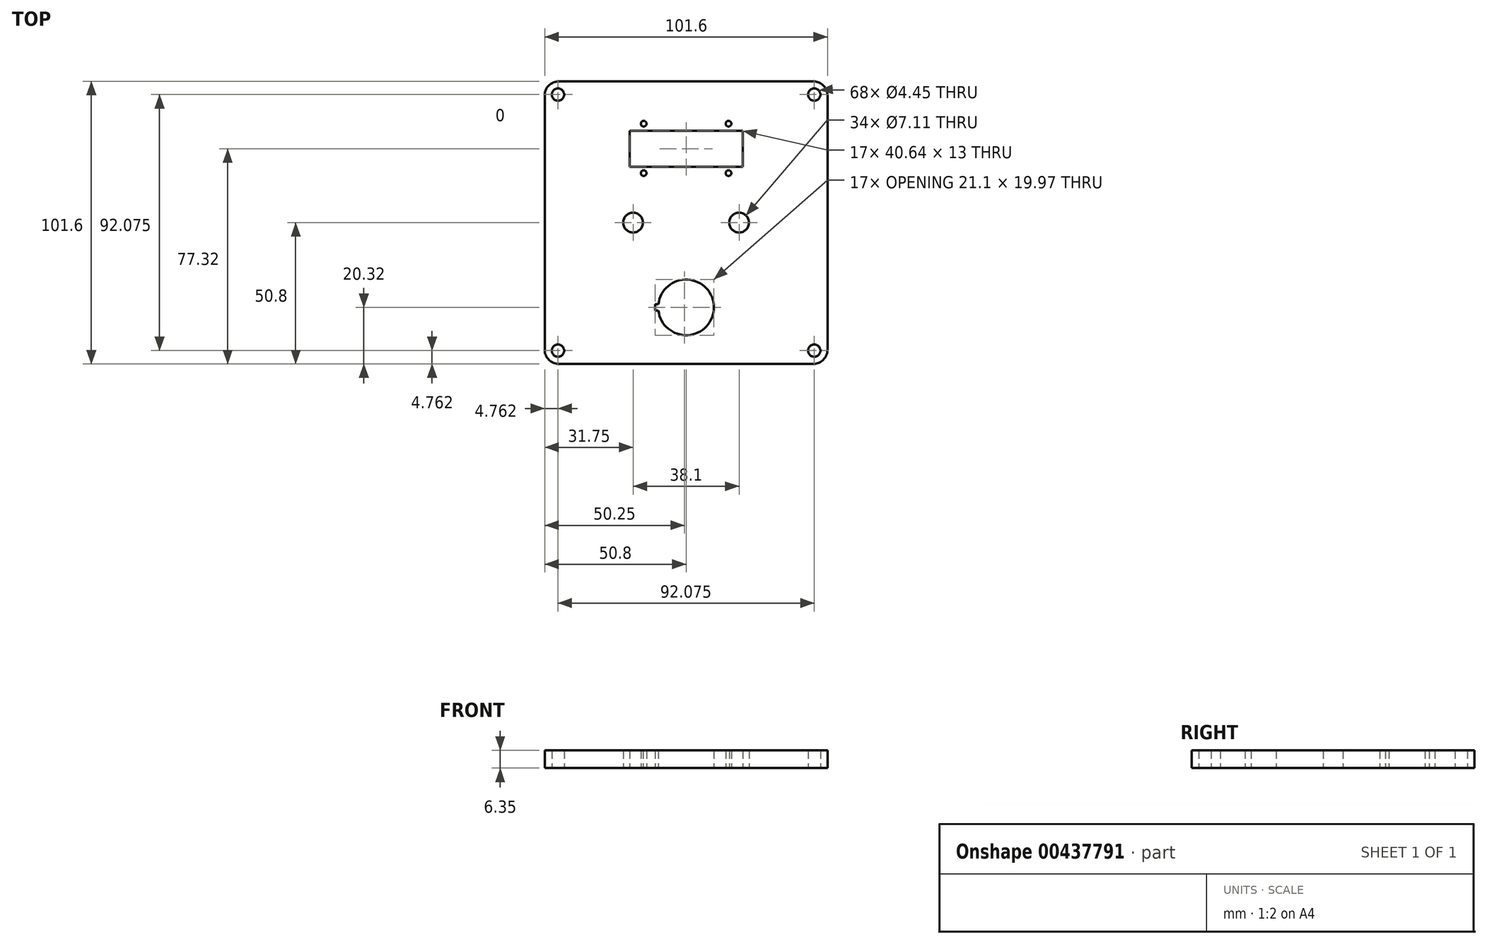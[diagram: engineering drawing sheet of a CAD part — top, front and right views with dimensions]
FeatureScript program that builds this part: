
annotation { "Feature Type Name" : "Feature", "Feature Type Description" : "" }
export const myFeature = defineFeature(function(context is Context, id is Id, definition is map)
    precondition{}
    {
        {
            var Q0;
            Q0=qCreatedBy(makeId("Top.planeOp"),FACE);
            var sketch = newSketch(context, id + "F0", { "sketchPlane" : qUnion([Q0])});
            skLineSegment(sketch, "E0.bottom", {"start": v(-45.72, 50.8) * mm, "end": v(45.72, 50.8) * mm});
            skLineSegment(sketch, "E0.top", {"start": v(-45.72, -50.8) * mm, "end": v(45.72, -50.8) * mm});
            skLineSegment(sketch, "E0.left", {"start": v(-50.8, 45.72) * mm, "end": v(-50.8, -45.72) * mm});
            skLineSegment(sketch, "E0.right", {"start": v(50.8, 45.72) * mm, "end": v(50.8, -45.72) * mm});
            skCircle(sketch, "E1", {"center": v(-46.04, 46.04) * mm, "radius": 2.22 * mm});
            skCircle(sketch, "E2.0.1.0", {"center": v(-46.04, -46.04) * mm, "radius": 2.22 * mm});
            skCircle(sketch, "E2.1.0.0", {"center": v(46.04, 46.04) * mm, "radius": 2.22 * mm});
            skCircle(sketch, "E2.1.1.0", {"center": v(46.04, -46.04) * mm, "radius": 2.22 * mm});
            skLineSegment(sketch, "E2.direction1", {"start": v(-46.04, 46.04) * mm, "end": v(46.04, 46.04) * mm, "construction": true});
            skLineSegment(sketch, "E2.direction2", {"start": v(-46.04, 46.04) * mm, "end": v(-46.04, -46.04) * mm, "construction": true});
            skArc(sketch, "E3", {"start": v(-9.94, -31.58) * mm, "mid": v(10, -30.48) * mm, "end": v(-9.94, -29.38) * mm});
            skLineSegment(sketch, "E4", {"start": v(0, -30.48) * mm, "end": v(-23.51, -30.48) * mm, "construction": true});
            skLineSegment(sketch, "E5", {"start": v(-11.1, -30.48) * mm, "end": v(-11.1, -29.38) * mm});
            skLineSegment(sketch, "E6", {"start": v(-11.1, -29.38) * mm, "end": v(-9.94, -29.38) * mm});
            skLineSegment(sketch, "E7.MirrorCS", {"start": v(-11.1, -30.48) * mm, "end": v(-11.1, -31.58) * mm});
            skLineSegment(sketch, "E8.MirrorCS", {"start": v(-11.1, -31.58) * mm, "end": v(-9.94, -31.58) * mm});
            skPoint(sketch, "E9", {"position": v(-50.8, 0) * mm});
            skPoint(sketch, "E10", {"position": v(0, 50.8) * mm});
            skPoint(sketch, "E11.visualSharp", {"position": v(-50.8, 50.8) * mm});
            skArc(sketch, "E11.filletArc", {"start": v(-45.72, 50.8) * mm, "mid": v(-49.31, 49.31) * mm, "end": v(-50.8, 45.72) * mm});
            skPoint(sketch, "E12.visualSharp", {"position": v(50.8, 50.8) * mm});
            skArc(sketch, "E12.filletArc", {"start": v(50.8, 45.72) * mm, "mid": v(49.31, 49.31) * mm, "end": v(45.72, 50.8) * mm});
            skPoint(sketch, "E13.visualSharp", {"position": v(50.8, -50.8) * mm});
            skArc(sketch, "E13.filletArc", {"start": v(45.72, -50.8) * mm, "mid": v(49.31, -49.31) * mm, "end": v(50.8, -45.72) * mm});
            skPoint(sketch, "E14.visualSharp", {"position": v(-50.8, -50.8) * mm});
            skArc(sketch, "E14.filletArc", {"start": v(-50.8, -45.72) * mm, "mid": v(-49.31, -49.31) * mm, "end": v(-45.72, -50.8) * mm});
            skCircle(sketch, "E15", {"center": v(-19.05, 0) * mm, "radius": 3.56 * mm});
            skCircle(sketch, "E16.0.1.0", {"center": v(-15.24, 17.78) * mm, "radius": 1.02 * mm});
            skLineSegment(sketch, "E17.bottom", {"start": v(20.32, 20.02) * mm, "end": v(-20.32, 20.02) * mm});
            skLineSegment(sketch, "E17.top", {"start": v(20.32, 33.02) * mm, "end": v(-20.32, 33.02) * mm});
            skLineSegment(sketch, "E17.left", {"start": v(20.32, 20.02) * mm, "end": v(20.32, 33.02) * mm});
            skLineSegment(sketch, "E17.right", {"start": v(-20.32, 20.02) * mm, "end": v(-20.32, 33.02) * mm});
            skPoint(sketch, "E18", {"position": v(0, 33.02) * mm});
            skPoint(sketch, "E19", {"position": v(0, 20.02) * mm});
            skCircle(sketch, "E20.MirrorC", {"center": v(19.05, 0) * mm, "radius": 3.56 * mm});
            skLineSegment(sketch, "E21", {"start": v(-20.32, 38.1) * mm, "end": v(-20.32, 15.24) * mm, "construction": true});
            skLineSegment(sketch, "E22", {"start": v(-20.32, 15.24) * mm, "end": v(20.32, 15.24) * mm, "construction": true});
            skLineSegment(sketch, "E23", {"start": v(20.32, 15.24) * mm, "end": v(20.32, 38.1) * mm, "construction": true});
            skLineSegment(sketch, "E24", {"start": v(20.32, 38.1) * mm, "end": v(-20.32, 38.1) * mm, "construction": true});
            skPoint(sketch, "E25", {"position": v(0, 15.24) * mm});
            skLineSegment(sketch, "E26", {"start": v(0, 0) * mm, "end": v(0, 117.68) * mm, "construction": true});
            skCircle(sketch, "E27.MirrorC", {"center": v(15.24, 17.78) * mm, "radius": 1.02 * mm});
            skLineSegment(sketch, "E28.direction2", {"start": v(-15.24, 17.78) * mm, "end": v(-15.24, 35.56) * mm, "construction": true});
            skPoint(sketch, "E29", {"position": v(-20.32, 26.67) * mm});
            skPoint(sketch, "E30", {"position": v(20.32, 26.67) * mm});
            skLineSegment(sketch, "E31", {"start": v(-20.32, 26.67) * mm, "end": v(20.32, 26.67) * mm, "construction": true});
            skCircle(sketch, "E32.MirrorC", {"center": v(-15.24, 35.56) * mm, "radius": 1.02 * mm});
            skCircle(sketch, "E33.MirrorC", {"center": v(15.24, 35.56) * mm, "radius": 1.02 * mm});
            skSolve(sketch);
        }
        {
            var Q0;
            Q0=makeQuery(id+"F0.imprint","IMPRINT",FACE,{"disambiguationData":[TD([[makeQuery(id+"F0.imprint","IMPRINT",EDGE,{"derivedFrom":sQuery(id+"F0.wireOp",EDGE,"E0.bottom")}),-1.0]])]});
            extrude(context, id + "F1", {"entities" : qUnion([Q0]), "depth" : 6.35 * mm});
        }
    });
